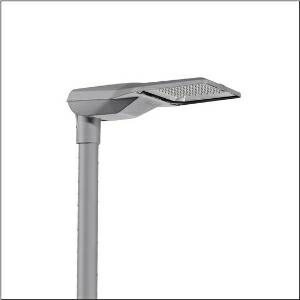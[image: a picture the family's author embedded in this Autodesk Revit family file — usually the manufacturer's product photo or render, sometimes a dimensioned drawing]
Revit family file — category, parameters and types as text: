
# Revit family: streetlight_sl_21_iq_midi___st0_5a_5xe3b31d08nb_970f
name_source: partatom
category: Lighting Fixtures
units: mm (PartAtom-declared; Revit-internal decimal feet)

## family parameters
Cut with Voids When Loaded = No
Host = Face
Light Source = No
Part Type = Normal
Room Calculation Point = No
Round Connector Dimension = Use Diameter
Shared = No

## types (1)
- --- (1 x LED, 23230 lm, 155.5 W, 3000K)
    Apparent Load = 155 VA
    CIE Flux Codes = 43 76 97 100 100
    Color Rendering = 70
    Color Temperature = 3000K
    Default Elevation = 1800 mm
    Description = Streetlight SL 21 iQ midi, mast luminaire, primary light control with lens, of PMMA, primary optical cover: cover, of toughened safety glass, transparent, light distribution: ST0.5a, light emission: direct distribution, primary light characteristic: asymmetric, installation type: post-top, side-entry, LED, High Power LED, rated luminous flux: 23.230lm, luminous efficacy: 149lm/W, light colour: 730, colour temperature: 3000K, control gear: iQ-Comfort, control: Auto-Match, Temp-Guard, Lumen-Switch, Night-Set, Smart-Wire, Light-Fading, Desk-Remote (wireless, voltage-free reading and setting of iQ features in the workshop via application-optimized NFC function/RFID function), optimised constant luminous flux control (CLO 2.0), pre-setting: linear dimming characteristic, mains connection: 230..240V, AC, 50/60Hz, start of lifetime: 156W, end of service life: 162W, reduction: 69W, luminaire housing, of diecast aluminium, powder-coated, SITECO metallic grey (DB 702S), corrosivity category C5 high according to DIN EN ISO 12944, please order mast flange separately, inclination adjustable: 0°, 5°, 10°, 15°, sealing non-destructively replaceable, multi-level sealing system, length: 644mm, width: 335mm, height: 110mm, mast flange for spigot size: 42mm (side-entry): 5XC10008XM4, 60/48mm (side-entry/post-top): 5XC10108XM2, 76/60mm (side-entry/post-top): 5XC10108XM1, mounting height: 4..8m, protection rating (complete): IP66, insulation class (complete): insulation class II (safety insulation), certification: CE, ENEC, ENEC+, VDE, impact resistance: IK10, permissible operating ambient temperature for outdoor applications: -40..+50°C, standard-compliant lighting for roads and squares, packaging unit: 1 piece

Light Distribution: ST0.5a
    Height = 111 mm
    Lamp = 1 x LED
    Lamp Light Flux = 23230 lm
    Lamp Power = 155.5 W
    Lamp count = 1
    Length = 644 mm
    Luminous efficacy = 149 lm/W
    Manufacturer = Siteco
    ModVariant = No
    Model = 5XE3B31D08NB
    Number of Poles = 1
    OnlyDefault = Yes
    Power Factor = 1
    Product Name = Streetlight SL 21 iQ midi | ST0.5a
    Product group = mast luminaire | pylon top
    ProductGroupID = 6100
    Protection Class = Protection class II
    Protection Degree = IP 66
    RLX_Detail_Level = 1
    RLX_Emergency_Light_Flux = 0 lm
    RLX_Emergency_Type = 0
    RLX_Emergency_Type_DB = No
    RlxData = <blob elided: 38341 chars, md5=a4d1d474>
    Socket = socket
    Standby Power = 0 W
    System Light Flux = 23230 lm
    System Power = 155 W
    Type Comments = factory setting: luminous flux: 100 % | dim-lin: 254 | 823 mA
    Type Image = l_1004298.jpg
    URL = http://relux.com
    VarID = @adj_171063
    Voltage = 0 V
    Weight = 0.00 kg
    Width = 336 mm

## geometry (parser evidence)
native form markers: Blend x4, Sweep x10
no freeform markers — native parametric forms only
